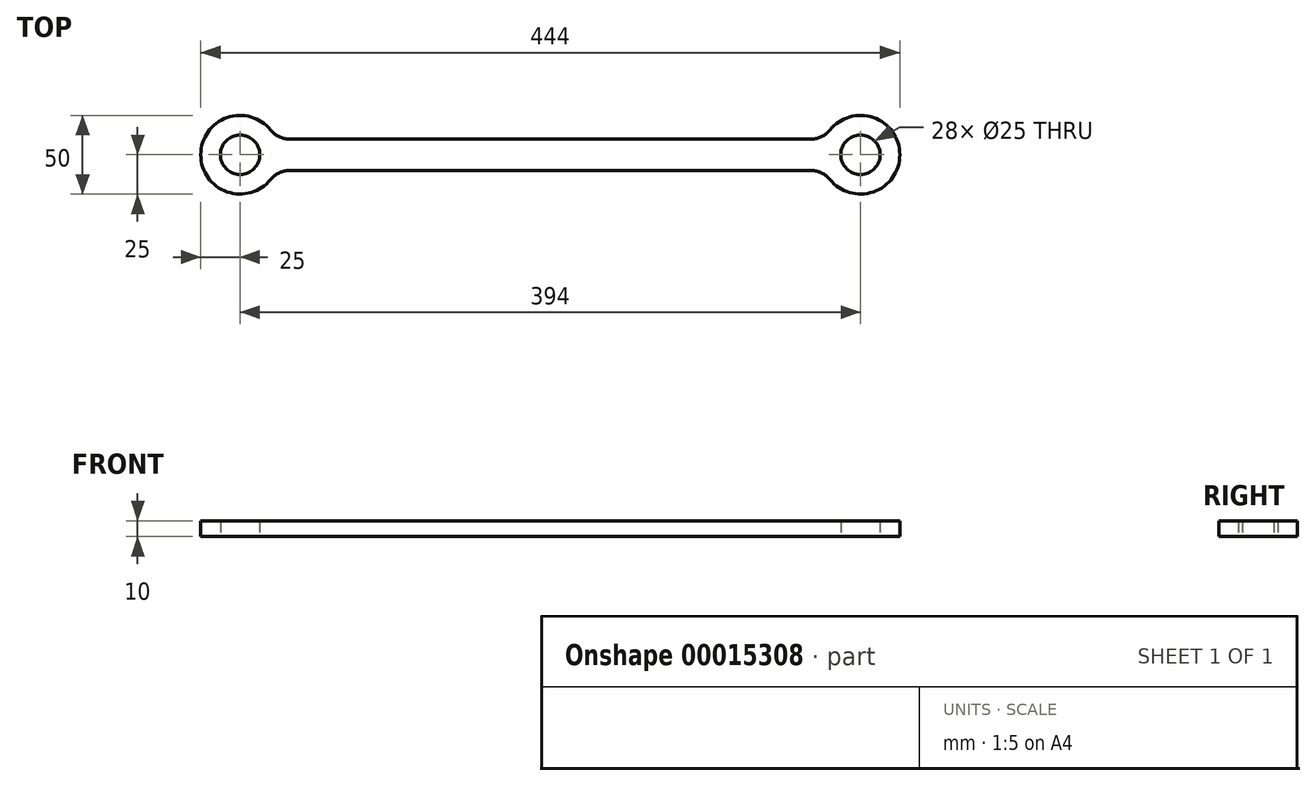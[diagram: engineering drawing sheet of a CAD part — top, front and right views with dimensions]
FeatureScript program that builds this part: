
annotation { "Feature Type Name" : "Feature", "Feature Type Description" : "" }
export const myFeature = defineFeature(function(context is Context, id is Id, definition is map)
    precondition{}
    {
        {
            var Q0;
            Q0=qCreatedBy(makeId("Top.planeOp"),FACE);
            var sketch = newSketch(context, id + "F0", { "sketchPlane" : qUnion([Q0])});
            skArc(sketch, "E0", {"start": v(19.52, 15.63) * mm, "mid": v(-25, 0) * mm, "end": v(19.52, -15.63) * mm});
            skArc(sketch, "E1", {"start": v(374.48, -15.63) * mm, "mid": v(419, 0) * mm, "end": v(374.48, 15.63) * mm});
            skLineSegment(sketch, "E2", {"start": v(31.22, 10) * mm, "end": v(362.78, 10) * mm});
            skLineSegment(sketch, "E3", {"start": v(0, 0) * mm, "end": v(394, 0) * mm, "construction": true});
            skLineSegment(sketch, "E4.MirrorCS", {"start": v(31.22, -10) * mm, "end": v(362.78, -10) * mm});
            skPoint(sketch, "E5.visualSharp", {"position": v(22.91, 10) * mm});
            skArc(sketch, "E5.filletArc", {"start": v(19.52, 15.62) * mm, "mid": v(24.73, 11.48) * mm, "end": v(31.22, 10) * mm});
            skPoint(sketch, "E6.visualSharp", {"position": v(22.91, -10) * mm});
            skArc(sketch, "E6.filletArc", {"start": v(31.22, -10) * mm, "mid": v(24.73, -11.48) * mm, "end": v(19.52, -15.62) * mm});
            skPoint(sketch, "E7.visualSharp", {"position": v(371.09, -10) * mm});
            skArc(sketch, "E7.filletArc", {"start": v(374.48, -15.63) * mm, "mid": v(369.27, -11.48) * mm, "end": v(362.78, -10) * mm});
            skPoint(sketch, "E8.visualSharp", {"position": v(371.09, 10) * mm});
            skArc(sketch, "E8.filletArc", {"start": v(362.78, 10) * mm, "mid": v(369.27, 11.48) * mm, "end": v(374.48, 15.63) * mm});
            skCircle(sketch, "E9", {"center": v(0, 0) * mm, "radius": 12.5 * mm});
            skCircle(sketch, "E10", {"center": v(394, 0) * mm, "radius": 12.5 * mm});
            skSolve(sketch);
        }
        {
            var Q0;
            Q0=qSketchRegion(id+"F0",true);
            extrude(context, id + "F1", {"entities" : qUnion([Q0]), "depth" : 10 * mm});
        }
    });
